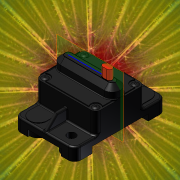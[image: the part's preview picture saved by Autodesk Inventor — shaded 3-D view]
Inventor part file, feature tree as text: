
AUTODESK INVENTOR PART (.ipt)
format: ipt  version: unknown  size: 1,178,624 bytes
history: native  units: mm (DEFAULTED — no unit token found)
features: sketch x21, extrude x13, fillet x9, emboss x5, mirror x4, chamfer x2, plane x2, reference x2, hole x1, projected_geometry x1
ambient origin geometry x8: Origin, YZ Plane, XZ Plane, XY Plane, X Axis, Y Axis, Z Axis, Center Point
bodies: Solid1 (feature_tree)
feature tree (60):
  extrude  "Extrusion1"  Depth=73.406mm
  fillet  "Fillet1"  Radius=24.13mm
  extrude  "Extrusion2"  Depth=5.08mm TaperAngle=0.0deg
  fillet  "Fillet2"  Radius=5.08mm
  hole  "Hole1"  [1 undecoded]
  extrude  "Extrusion3"  Depth=10.795mm
  mirror  "Mirror3"
  mirror  "Mirror4"
  extrude  "Extrusion4"  Depth=14.224mm
  fillet  "Fillet3"  Radius=14.224mm
  chamfer  "Chamfer1"  Distance=5.08mm
  extrude  "Button"  Depth=8.89mm TaperAngle=0.0deg
  fillet  "Fillet4"  Radius=6.477mm
  fillet  "Fillet7"  Radius=3.81mm
  extrude  "Extrusion6"  Depth=7.62mm
  chamfer  "Chamfer2"  Distance=7.62mm
  fillet  "Fillet5"  Radius=2.159mm
  mirror  "Mirror5"
  fillet  "Fillet6"  Radius=2.54mm
  extrude  "Extrusion7"  Depth=8.89mm TaperAngle=0.0deg
  extrude  "Extrusion8"  Depth=1.27mm
  fillet  "Fillet8"  Radius=1.27mm
  sketch  "Sketch11"  dims[d38=1.27mm d39=8.89mm d40=0.0mm]
  plane  "Work Plane1"
  sketch  "Sketch12"  dims[d41=8.89mm d42=8.89mm d43=1.27mm d44=1.27mm d45=0.635mm]
  plane  "Work Plane2"
  mirror  "Mirror7"
  fillet  "Fillet9"  Radius=0.635mm
  extrude  "Extrusion9"  TaperAngle=45.0deg  [1 undecoded]
  extrude  "Extrusion10"  Depth=1.27mm
  emboss  "Emboss1"
  extrude  "Extrusion11"  Depth=0.762mm TaperAngle=0.0deg
  emboss  "Emboss2"
  extrude  "Extrusion12"  Depth=5.08mm
  emboss  "Emboss3"
  emboss  "Emboss4"
  emboss  "Emboss5"
  extrude  "Extrusion13"  Depth=2.54mm
  sketch  "Sketch1"  dims[d0=48.26mm d1=73.406mm d2=24.13mm]
  sketch  "Sketch2"  dims[d3=36.703mm d4=5.08mm d5=0.0mm d6=5.08mm]
  sketch  "Sketch3"  dims[d7=39.37mm d8=17.526mm d9=0.0mm]
  sketch  "Sketch5"  dims[d10=3.81mm d11=10.795mm]
  sketch  "Sketch6"  dims[d12=8.382mm]
  sketch  "Sketch7"  dims[d13=6.604mm d14=12.7mm d15=9.525mm d16=6.35mm d17=14.3117mm d18=19.05mm d19=20.594885mm d20=14.224mm d21=14.224mm d23=5.08mm d24=0.0mm]
  sketch  "Sketch8"  dims[d25=12.954mm d26=8.89mm d27=0.0mm d28=6.477mm d29=3.81mm d30=3.81mm]
  sketch  "Sketch9"  dims[d31=4.318mm d32=7.62mm]
  projected_geometry  "Projected Loop1"
  sketch  "Sketch10"  dims[d33=2.159mm d34=7.62mm d35=0.0mm d36=2.159mm d37=2.54mm]
  sketch  "Sketch13"  dims[d46=1.27mm d47=45.0deg d48=45.0deg]
  reference  "Reference1"
  sketch  "Sketch14"  dims[d52=1.27mm d53=1.27mm]
  reference  "Reference2"
  sketch  "Sketch15"  dims[d54=1.27mm d55=0.762mm d56=0.0mm]
  sketch  "Sketch16"  dims[d57=5.08mm d58=5.08mm]
  sketch  "Sketch17"  dims[d59=0.762mm d60=0.0mm d61=2.54mm]
  sketch  "Sketch18"  dims[d62=90.0deg d63=2.54mm]
  sketch  "Sketch19"  dims[d64=0.508mm d65=0.0mm]
  sketch  "Sketch20"  dims[d66=0.508mm d67=0.0mm]
  sketch  "Sketch21"  dims[d68=0.254mm d69=0.0mm]
  sketch  "Sketch22"  dims[d70=0.0254mm d71=0.0mm d72=0.254mm d73=0.0mm d74=0.0508mm d75=0.5334mm d76=0.254mm d77=0.0mm d78=0.0254mm d79=0.0mm d80=0.0254mm d81=0.0mm d82=0.0254mm d83=0.0mm d84=2.54mm d85=2.54mm d86=0.0254mm d87=0.0mm]
note: 2 required parameter values undecoded (feature->parameter linkage not recoverable at this tier; creation-order binding heuristic only, values carry confidence <= 0.55)
